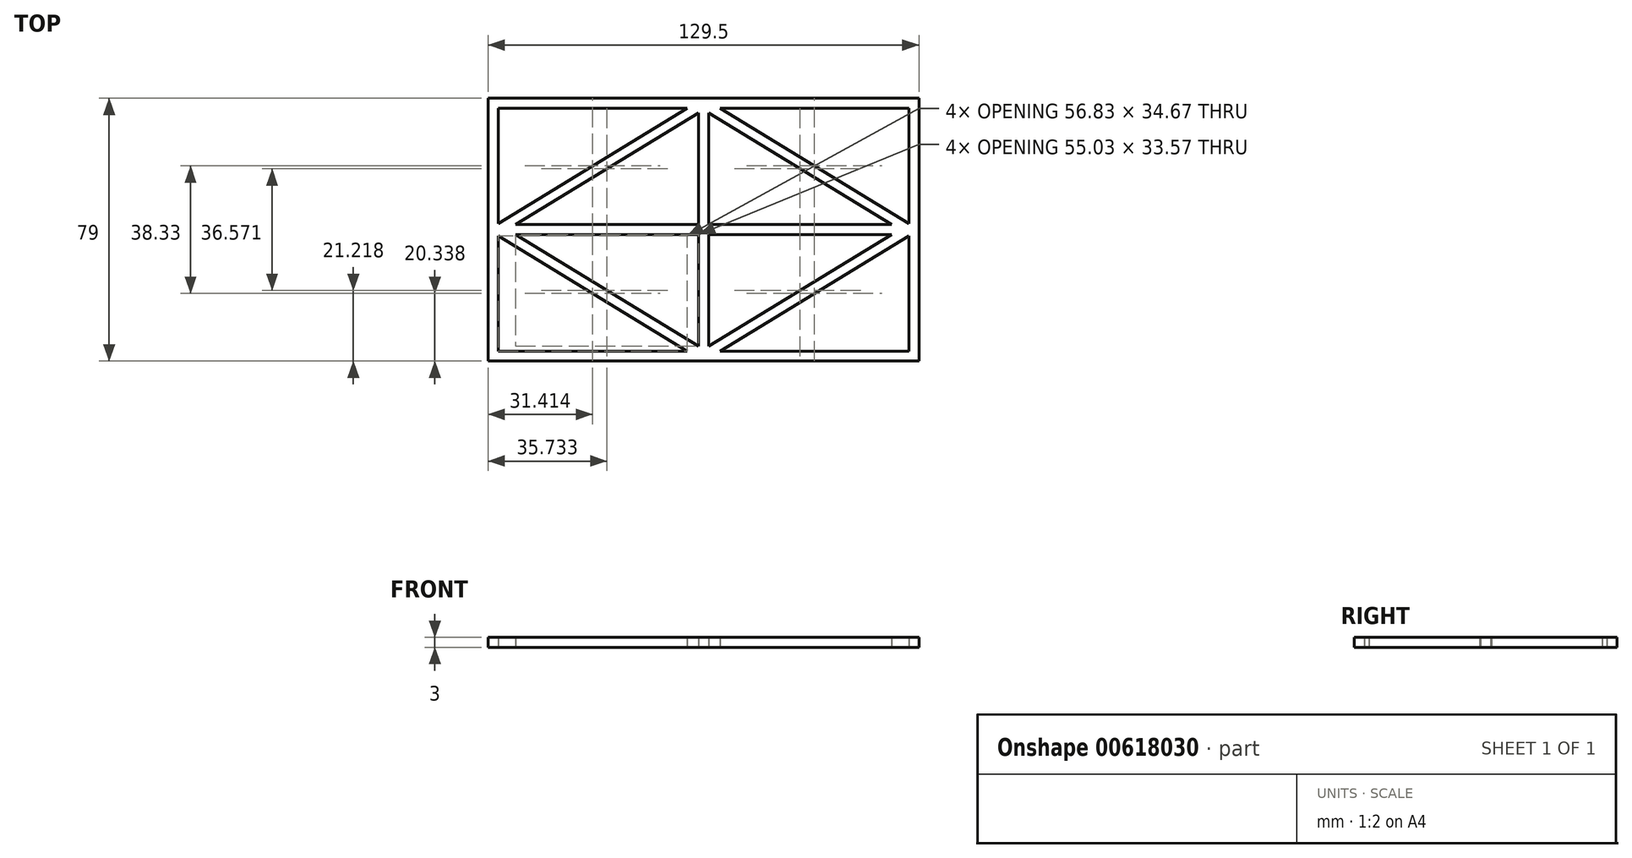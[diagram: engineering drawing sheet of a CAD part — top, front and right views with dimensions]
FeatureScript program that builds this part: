
annotation { "Feature Type Name" : "Feature", "Feature Type Description" : "" }
export const myFeature = defineFeature(function(context is Context, id is Id, definition is map)
    precondition{}
    {
        {
            var Q0;
            Q0=qCreatedBy(makeId("Top.planeOp"),FACE);
            var sketch = newSketch(context, id + "F0", { "sketchPlane" : qUnion([Q0])});
            skLineSegment(sketch, "E0.bottom", {"start": v(-93.35, 45.57) * mm, "end": v(36.15, 45.57) * mm});
            skLineSegment(sketch, "E0.top", {"start": v(-93.35, -33.43) * mm, "end": v(36.15, -33.43) * mm});
            skLineSegment(sketch, "E0.left", {"start": v(-93.35, 45.57) * mm, "end": v(-93.35, -33.43) * mm});
            skLineSegment(sketch, "E0.right", {"start": v(36.15, 45.57) * mm, "end": v(36.15, -33.43) * mm});
            skLineSegment(sketch, "E1", {"start": v(-28.6, 45.57) * mm, "end": v(-28.6, -33.43) * mm});
            skLineSegment(sketch, "E2", {"start": v(-28.6, -33.43) * mm, "end": v(-93.35, 6.07) * mm});
            skLineSegment(sketch, "E3", {"start": v(-93.35, 6.07) * mm, "end": v(-28.6, 45.57) * mm});
            skLineSegment(sketch, "E4", {"start": v(-28.6, 45.57) * mm, "end": v(36.15, 6.07) * mm});
            skLineSegment(sketch, "E5", {"start": v(36.15, 6.07) * mm, "end": v(-28.6, -33.43) * mm});
            skLineSegment(sketch, "E6", {"start": v(36.15, 6.07) * mm, "end": v(-93.35, 6.07) * mm});
            skLineSegment(sketch, "E7.0", {"start": v(-30.1, 45.57) * mm, "end": v(-30.1, -33.43) * mm});
            skLineSegment(sketch, "E8.0", {"start": v(-27.1, 45.57) * mm, "end": v(-27.1, -33.43) * mm});
            skLineSegment(sketch, "E9.0", {"start": v(36.15, 7.57) * mm, "end": v(-93.35, 7.57) * mm});
            skLineSegment(sketch, "E10.0", {"start": v(36.15, 4.57) * mm, "end": v(-93.35, 4.57) * mm});
            skLineSegment(sketch, "E11.0", {"start": v(-90.35, 42.57) * mm, "end": v(33.15, 42.57) * mm});
            skLineSegment(sketch, "E11.1", {"start": v(-90.35, 42.57) * mm, "end": v(-90.35, -30.43) * mm});
            skLineSegment(sketch, "E11.2", {"start": v(-90.35, -30.43) * mm, "end": v(33.15, -30.43) * mm});
            skLineSegment(sketch, "E11.3", {"start": v(33.15, 42.57) * mm, "end": v(33.15, -30.43) * mm});
            skLineSegment(sketch, "E12.0", {"start": v(-87.6, 6.07) * mm, "end": v(-28.6, 42.06) * mm});
            skLineSegment(sketch, "E12.1", {"start": v(-28.6, -29.91) * mm, "end": v(-87.6, 6.07) * mm});
            skLineSegment(sketch, "E12.2", {"start": v(30.39, 6.07) * mm, "end": v(-28.6, -29.91) * mm});
            skLineSegment(sketch, "E12.3", {"start": v(-28.6, 42.06) * mm, "end": v(30.39, 6.07) * mm});
            skSolve(sketch);
        }
        {
            var Q0;
            {var subQ8=sQuery(id+"F0.wireOp",EDGE,"E0.left");var subQ9=sQuery(id+"F0.wireOp",EDGE,"E0.bottom");var subQ10=makeQuery(id+"F0.imprint","INTERSECT",VERTEX,{"derivedFrom":[subQ9,subQ8]});Q0=makeQuery(id+"F0.imprint","IMPRINT",FACE,{"disambiguationData":[TD([[makeQuery(id+"F0.imprint","IMPRINT",EDGE,{"disambiguationData":[TD([[subQ10,-1.0]])],"derivedFrom":subQ9}),-1.0]])]});}
            var Q1;
            {var subQ1=sQuery(id+"F0.wireOp",EDGE,"E3");var subQ8=sQuery(id+"F0.wireOp",EDGE,"E11.1");var subQ11=makeQuery(id+"F0.imprint","INTERSECT",VERTEX,{"derivedFrom":[subQ1,subQ8]});Q1=makeQuery(id+"F0.imprint","IMPRINT",FACE,{"disambiguationData":[TD([[makeQuery(id+"F0.imprint","IMPRINT",EDGE,{"disambiguationData":[TD([[subQ11,-1.0]])],"derivedFrom":subQ1}),-1.0]])]});}
            var Q2;
            {var subQ1=sQuery(id+"F0.wireOp",EDGE,"E0.bottom");var subQ3=sQuery(id+"F0.wireOp",EDGE,"E7.0");var subQ4=makeQuery(id+"F0.imprint","INTERSECT",VERTEX,{"derivedFrom":[subQ1,subQ3]});Q2=makeQuery(id+"F0.imprint","IMPRINT",FACE,{"disambiguationData":[TD([[makeQuery(id+"F0.imprint","IMPRINT",EDGE,{"disambiguationData":[TD([[subQ4,-1.0]])],"derivedFrom":subQ3}),1.0]])]});}
            var Q3;
            {var subQ0=sQuery(id+"F0.wireOp",EDGE,"E3");var subQ5=sQuery(id+"F0.wireOp",EDGE,"E7.0");var subQ6=makeQuery(id+"F0.imprint","INTERSECT",VERTEX,{"derivedFrom":[subQ0,subQ5]});Q3=makeQuery(id+"F0.imprint","IMPRINT",FACE,{"disambiguationData":[TD([[makeQuery(id+"F0.imprint","IMPRINT",EDGE,{"disambiguationData":[TD([[subQ6,-1.0]])],"derivedFrom":subQ5}),1.0]])]});}
            var Q4;
            {var subQ0=sQuery(id+"F0.wireOp",EDGE,"E11.0");var subQ1=sQuery(id+"F0.wireOp",EDGE,"E3");var subQ2=makeQuery(id+"F0.imprint","INTERSECT",VERTEX,{"derivedFrom":[subQ1,subQ0]});Q4=makeQuery(id+"F0.imprint","IMPRINT",FACE,{"disambiguationData":[TD([[makeQuery(id+"F0.imprint","IMPRINT",EDGE,{"disambiguationData":[TD([[subQ2,-1.0]])],"derivedFrom":subQ1}),-1.0]])]});}
            var Q5;
            {var subQ3=sQuery(id+"F0.wireOp",EDGE,"E11.0");var subQ5=sQuery(id+"F0.wireOp",EDGE,"E7.0");var subQ6=makeQuery(id+"F0.imprint","INTERSECT",VERTEX,{"derivedFrom":[subQ5,subQ3]});Q5=makeQuery(id+"F0.imprint","IMPRINT",FACE,{"disambiguationData":[TD([[makeQuery(id+"F0.imprint","IMPRINT",EDGE,{"disambiguationData":[TD([[subQ6,-1.0]])],"derivedFrom":subQ5}),1.0]])]});}
            var Q6;
            {var subQ3=sQuery(id+"F0.wireOp",EDGE,"E11.0");var subQ5=sQuery(id+"F0.wireOp",EDGE,"E8.0");var subQ6=makeQuery(id+"F0.imprint","INTERSECT",VERTEX,{"derivedFrom":[subQ5,subQ3]});Q6=makeQuery(id+"F0.imprint","IMPRINT",FACE,{"disambiguationData":[TD([[makeQuery(id+"F0.imprint","IMPRINT",EDGE,{"disambiguationData":[TD([[subQ6,-1.0]])],"derivedFrom":subQ5}),-1.0]])]});}
            var Q7;
            {var subQ0=sQuery(id+"F0.wireOp",EDGE,"E4");var subQ5=sQuery(id+"F0.wireOp",EDGE,"E8.0");var subQ6=makeQuery(id+"F0.imprint","INTERSECT",VERTEX,{"derivedFrom":[subQ0,subQ5]});Q7=makeQuery(id+"F0.imprint","IMPRINT",FACE,{"disambiguationData":[TD([[makeQuery(id+"F0.imprint","IMPRINT",EDGE,{"disambiguationData":[TD([[subQ6,-1.0]])],"derivedFrom":subQ5}),-1.0]])]});}
            var Q8;
            {var subQ1=sQuery(id+"F0.wireOp",EDGE,"E0.bottom");var subQ3=sQuery(id+"F0.wireOp",EDGE,"E8.0");var subQ4=makeQuery(id+"F0.imprint","INTERSECT",VERTEX,{"derivedFrom":[subQ1,subQ3]});Q8=makeQuery(id+"F0.imprint","IMPRINT",FACE,{"disambiguationData":[TD([[makeQuery(id+"F0.imprint","IMPRINT",EDGE,{"disambiguationData":[TD([[subQ4,-1.0]])],"derivedFrom":subQ3}),-1.0]])]});}
            var Q9;
            {var subQ9=sQuery(id+"F0.wireOp",EDGE,"E0.right");var subQ10=sQuery(id+"F0.wireOp",EDGE,"E0.bottom");var subQ11=makeQuery(id+"F0.imprint","INTERSECT",VERTEX,{"derivedFrom":[subQ10,subQ9]});Q9=makeQuery(id+"F0.imprint","IMPRINT",FACE,{"disambiguationData":[TD([[makeQuery(id+"F0.imprint","IMPRINT",EDGE,{"disambiguationData":[TD([[subQ11,1.0]])],"derivedFrom":subQ10}),-1.0]])]});}
            var Q10;
            {var subQ0=sQuery(id+"F0.wireOp",EDGE,"E8.0");var subQ1=sQuery(id+"F0.wireOp",EDGE,"E4");var subQ2=makeQuery(id+"F0.imprint","INTERSECT",VERTEX,{"derivedFrom":[subQ1,subQ0]});Q10=makeQuery(id+"F0.imprint","IMPRINT",FACE,{"disambiguationData":[TD([[makeQuery(id+"F0.imprint","IMPRINT",EDGE,{"disambiguationData":[TD([[subQ2,-1.0]])],"derivedFrom":subQ1}),-1.0]])]});}
            var Q11;
            {var subQ5=sQuery(id+"F0.wireOp",EDGE,"E11.0");var subQ6=sQuery(id+"F0.wireOp",EDGE,"E4");var subQ7=makeQuery(id+"F0.imprint","INTERSECT",VERTEX,{"derivedFrom":[subQ6,subQ5]});Q11=makeQuery(id+"F0.imprint","IMPRINT",FACE,{"disambiguationData":[TD([[makeQuery(id+"F0.imprint","IMPRINT",EDGE,{"disambiguationData":[TD([[subQ7,-1.0]])],"derivedFrom":subQ6}),-1.0]])]});}
            var Q12;
            {var subQ0=sQuery(id+"F0.wireOp",EDGE,"E12.0");var subQ5=sQuery(id+"F0.wireOp",EDGE,"E7.0");var subQ6=makeQuery(id+"F0.imprint","INTERSECT",VERTEX,{"derivedFrom":[subQ5,subQ0]});Q12=makeQuery(id+"F0.imprint","IMPRINT",FACE,{"disambiguationData":[TD([[makeQuery(id+"F0.imprint","IMPRINT",EDGE,{"disambiguationData":[TD([[subQ6,-1.0]])],"derivedFrom":subQ5}),1.0]])]});}
            var Q13;
            {var subQ0=sQuery(id+"F0.wireOp",EDGE,"E12.3");var subQ5=sQuery(id+"F0.wireOp",EDGE,"E8.0");var subQ6=makeQuery(id+"F0.imprint","INTERSECT",VERTEX,{"derivedFrom":[subQ5,subQ0]});Q13=makeQuery(id+"F0.imprint","IMPRINT",FACE,{"disambiguationData":[TD([[makeQuery(id+"F0.imprint","IMPRINT",EDGE,{"disambiguationData":[TD([[subQ6,-1.0]])],"derivedFrom":subQ5}),-1.0]])]});}
            var Q14;
            {var subQ1=sQuery(id+"F0.wireOp",EDGE,"E6");var subQ3=sQuery(id+"F0.wireOp",EDGE,"E7.0");var subQ4=makeQuery(id+"F0.imprint","INTERSECT",VERTEX,{"derivedFrom":[subQ1,subQ3]});Q14=makeQuery(id+"F0.imprint","IMPRINT",FACE,{"disambiguationData":[TD([[makeQuery(id+"F0.imprint","IMPRINT",EDGE,{"disambiguationData":[TD([[subQ4,1.0]])],"derivedFrom":subQ3}),-1.0]])]});}
            var Q15;
            {var subQ1=sQuery(id+"F0.wireOp",EDGE,"E6");var subQ3=sQuery(id+"F0.wireOp",EDGE,"E7.0");var subQ4=makeQuery(id+"F0.imprint","INTERSECT",VERTEX,{"derivedFrom":[subQ1,subQ3]});Q15=makeQuery(id+"F0.imprint","IMPRINT",FACE,{"disambiguationData":[TD([[makeQuery(id+"F0.imprint","IMPRINT",EDGE,{"disambiguationData":[TD([[subQ4,-1.0]])],"derivedFrom":subQ3}),-1.0]])]});}
            var Q16;
            {var subQ0=sQuery(id+"F0.wireOp",EDGE,"E9.0");var subQ1=sQuery(id+"F0.wireOp",EDGE,"E1");var subQ2=makeQuery(id+"F0.imprint","INTERSECT",VERTEX,{"derivedFrom":[subQ1,subQ0]});Q16=makeQuery(id+"F0.imprint","IMPRINT",FACE,{"disambiguationData":[TD([[makeQuery(id+"F0.imprint","IMPRINT",EDGE,{"disambiguationData":[TD([[subQ2,-1.0]])],"derivedFrom":subQ1}),-1.0]])]});}
            var Q17;
            {var subQ0=sQuery(id+"F0.wireOp",EDGE,"E9.0");var subQ1=sQuery(id+"F0.wireOp",EDGE,"E1");var subQ2=makeQuery(id+"F0.imprint","INTERSECT",VERTEX,{"derivedFrom":[subQ1,subQ0]});Q17=makeQuery(id+"F0.imprint","IMPRINT",FACE,{"disambiguationData":[TD([[makeQuery(id+"F0.imprint","IMPRINT",EDGE,{"disambiguationData":[TD([[subQ2,-1.0]])],"derivedFrom":subQ1}),1.0]])]});}
            var Q18;
            {var subQ0=sQuery(id+"F0.wireOp",EDGE,"E6");var subQ1=sQuery(id+"F0.wireOp",EDGE,"E1");var subQ2=makeQuery(id+"F0.imprint","INTERSECT",VERTEX,{"derivedFrom":[subQ1,subQ0]});Q18=makeQuery(id+"F0.imprint","IMPRINT",FACE,{"disambiguationData":[TD([[makeQuery(id+"F0.imprint","IMPRINT",EDGE,{"disambiguationData":[TD([[subQ2,-1.0]])],"derivedFrom":subQ1}),1.0]])]});}
            var Q19;
            {var subQ0=sQuery(id+"F0.wireOp",EDGE,"E6");var subQ1=sQuery(id+"F0.wireOp",EDGE,"E1");var subQ2=makeQuery(id+"F0.imprint","INTERSECT",VERTEX,{"derivedFrom":[subQ1,subQ0]});Q19=makeQuery(id+"F0.imprint","IMPRINT",FACE,{"disambiguationData":[TD([[makeQuery(id+"F0.imprint","IMPRINT",EDGE,{"disambiguationData":[TD([[subQ2,-1.0]])],"derivedFrom":subQ1}),-1.0]])]});}
            var Q20;
            {var subQ1=sQuery(id+"F0.wireOp",EDGE,"E6");var subQ3=sQuery(id+"F0.wireOp",EDGE,"E8.0");var subQ4=makeQuery(id+"F0.imprint","INTERSECT",VERTEX,{"derivedFrom":[subQ1,subQ3]});Q20=makeQuery(id+"F0.imprint","IMPRINT",FACE,{"disambiguationData":[TD([[makeQuery(id+"F0.imprint","IMPRINT",EDGE,{"disambiguationData":[TD([[subQ4,1.0]])],"derivedFrom":subQ3}),1.0]])]});}
            var Q21;
            {var subQ1=sQuery(id+"F0.wireOp",EDGE,"E6");var subQ3=sQuery(id+"F0.wireOp",EDGE,"E8.0");var subQ4=makeQuery(id+"F0.imprint","INTERSECT",VERTEX,{"derivedFrom":[subQ1,subQ3]});Q21=makeQuery(id+"F0.imprint","IMPRINT",FACE,{"disambiguationData":[TD([[makeQuery(id+"F0.imprint","IMPRINT",EDGE,{"disambiguationData":[TD([[subQ4,-1.0]])],"derivedFrom":subQ3}),1.0]])]});}
            var Q22;
            {var subQ3=sQuery(id+"F0.wireOp",EDGE,"E10.0");var subQ5=sQuery(id+"F0.wireOp",EDGE,"E8.0");var subQ6=makeQuery(id+"F0.imprint","INTERSECT",VERTEX,{"derivedFrom":[subQ5,subQ3]});Q22=makeQuery(id+"F0.imprint","IMPRINT",FACE,{"disambiguationData":[TD([[makeQuery(id+"F0.imprint","IMPRINT",EDGE,{"disambiguationData":[TD([[subQ6,-1.0]])],"derivedFrom":subQ5}),-1.0]])]});}
            var Q23;
            {var subQ3=sQuery(id+"F0.wireOp",EDGE,"E10.0");var subQ5=sQuery(id+"F0.wireOp",EDGE,"E7.0");var subQ6=makeQuery(id+"F0.imprint","INTERSECT",VERTEX,{"derivedFrom":[subQ5,subQ3]});Q23=makeQuery(id+"F0.imprint","IMPRINT",FACE,{"disambiguationData":[TD([[makeQuery(id+"F0.imprint","IMPRINT",EDGE,{"disambiguationData":[TD([[subQ6,-1.0]])],"derivedFrom":subQ5}),1.0]])]});}
            var Q24;
            {var subQ3=sQuery(id+"F0.wireOp",EDGE,"E11.3");var subQ5=sQuery(id+"F0.wireOp",EDGE,"E9.0");var subQ6=makeQuery(id+"F0.imprint","INTERSECT",VERTEX,{"derivedFrom":[subQ5,subQ3]});Q24=makeQuery(id+"F0.imprint","IMPRINT",FACE,{"disambiguationData":[TD([[makeQuery(id+"F0.imprint","IMPRINT",EDGE,{"disambiguationData":[TD([[subQ6,-1.0]])],"derivedFrom":subQ5}),1.0]])]});}
            var Q25;
            {var subQ0=sQuery(id+"F0.wireOp",EDGE,"E11.3");var subQ1=sQuery(id+"F0.wireOp",EDGE,"E4");var subQ2=makeQuery(id+"F0.imprint","INTERSECT",VERTEX,{"derivedFrom":[subQ1,subQ0]});Q25=makeQuery(id+"F0.imprint","IMPRINT",FACE,{"disambiguationData":[TD([[makeQuery(id+"F0.imprint","IMPRINT",EDGE,{"disambiguationData":[TD([[subQ2,-1.0]])],"derivedFrom":subQ1}),-1.0]])]});}
            var Q26;
            {var subQ1=sQuery(id+"F0.wireOp",EDGE,"E4");var subQ3=sQuery(id+"F0.wireOp",EDGE,"E9.0");var subQ4=makeQuery(id+"F0.imprint","INTERSECT",VERTEX,{"derivedFrom":[subQ1,subQ3]});Q26=makeQuery(id+"F0.imprint","IMPRINT",FACE,{"disambiguationData":[TD([[makeQuery(id+"F0.imprint","IMPRINT",EDGE,{"disambiguationData":[TD([[subQ4,-1.0]])],"derivedFrom":subQ3}),1.0]])]});}
            var Q27;
            {var subQ1=sQuery(id+"F0.wireOp",EDGE,"E0.right");var subQ3=sQuery(id+"F0.wireOp",EDGE,"E9.0");var subQ4=makeQuery(id+"F0.imprint","INTERSECT",VERTEX,{"derivedFrom":[subQ1,subQ3]});Q27=makeQuery(id+"F0.imprint","IMPRINT",FACE,{"disambiguationData":[TD([[makeQuery(id+"F0.imprint","IMPRINT",EDGE,{"disambiguationData":[TD([[subQ4,-1.0]])],"derivedFrom":subQ3}),1.0]])]});}
            var Q28;
            {var subQ1=sQuery(id+"F0.wireOp",EDGE,"E5");var subQ3=sQuery(id+"F0.wireOp",EDGE,"E10.0");var subQ4=makeQuery(id+"F0.imprint","INTERSECT",VERTEX,{"derivedFrom":[subQ1,subQ3]});Q28=makeQuery(id+"F0.imprint","IMPRINT",FACE,{"disambiguationData":[TD([[makeQuery(id+"F0.imprint","IMPRINT",EDGE,{"disambiguationData":[TD([[subQ4,-1.0]])],"derivedFrom":subQ3}),-1.0]])]});}
            var Q29;
            {var subQ1=sQuery(id+"F0.wireOp",EDGE,"E0.right");var subQ3=sQuery(id+"F0.wireOp",EDGE,"E10.0");var subQ4=makeQuery(id+"F0.imprint","INTERSECT",VERTEX,{"derivedFrom":[subQ1,subQ3]});Q29=makeQuery(id+"F0.imprint","IMPRINT",FACE,{"disambiguationData":[TD([[makeQuery(id+"F0.imprint","IMPRINT",EDGE,{"disambiguationData":[TD([[subQ4,-1.0]])],"derivedFrom":subQ3}),-1.0]])]});}
            var Q30;
            {var subQ3=sQuery(id+"F0.wireOp",EDGE,"E11.3");var subQ5=sQuery(id+"F0.wireOp",EDGE,"E10.0");var subQ6=makeQuery(id+"F0.imprint","INTERSECT",VERTEX,{"derivedFrom":[subQ5,subQ3]});Q30=makeQuery(id+"F0.imprint","IMPRINT",FACE,{"disambiguationData":[TD([[makeQuery(id+"F0.imprint","IMPRINT",EDGE,{"disambiguationData":[TD([[subQ6,-1.0]])],"derivedFrom":subQ5}),-1.0]])]});}
            var Q31;
            {var subQ1=sQuery(id+"F0.wireOp",EDGE,"E5");var subQ5=sQuery(id+"F0.wireOp",EDGE,"E11.3");var subQ11=makeQuery(id+"F0.imprint","INTERSECT",VERTEX,{"derivedFrom":[subQ1,subQ5]});Q31=makeQuery(id+"F0.imprint","IMPRINT",FACE,{"disambiguationData":[TD([[makeQuery(id+"F0.imprint","IMPRINT",EDGE,{"disambiguationData":[TD([[subQ11,-1.0]])],"derivedFrom":subQ1}),-1.0]])]});}
            var Q32;
            {var subQ0=sQuery(id+"F0.wireOp",EDGE,"E10.0");var subQ1=sQuery(id+"F0.wireOp",EDGE,"E5");var subQ2=makeQuery(id+"F0.imprint","INTERSECT",VERTEX,{"derivedFrom":[subQ1,subQ0]});Q32=makeQuery(id+"F0.imprint","IMPRINT",FACE,{"disambiguationData":[TD([[makeQuery(id+"F0.imprint","IMPRINT",EDGE,{"disambiguationData":[TD([[subQ2,-1.0]])],"derivedFrom":subQ1}),-1.0]])]});}
            var Q33;
            {var subQ5=sQuery(id+"F0.wireOp",EDGE,"E0.right");var subQ6=sQuery(id+"F0.wireOp",EDGE,"E0.top");var subQ7=makeQuery(id+"F0.imprint","INTERSECT",VERTEX,{"derivedFrom":[subQ6,subQ5]});Q33=makeQuery(id+"F0.imprint","IMPRINT",FACE,{"disambiguationData":[TD([[makeQuery(id+"F0.imprint","IMPRINT",EDGE,{"disambiguationData":[TD([[subQ7,1.0]])],"derivedFrom":subQ6}),1.0]])]});}
            var Q34;
            {var subQ1=sQuery(id+"F0.wireOp",EDGE,"E0.top");var subQ3=sQuery(id+"F0.wireOp",EDGE,"E8.0");var subQ4=makeQuery(id+"F0.imprint","INTERSECT",VERTEX,{"derivedFrom":[subQ1,subQ3]});Q34=makeQuery(id+"F0.imprint","IMPRINT",FACE,{"disambiguationData":[TD([[makeQuery(id+"F0.imprint","IMPRINT",EDGE,{"disambiguationData":[TD([[subQ4,1.0]])],"derivedFrom":subQ3}),-1.0]])]});}
            var Q35;
            {var subQ0=sQuery(id+"F0.wireOp",EDGE,"E5");var subQ5=sQuery(id+"F0.wireOp",EDGE,"E8.0");var subQ6=makeQuery(id+"F0.imprint","INTERSECT",VERTEX,{"derivedFrom":[subQ0,subQ5]});Q35=makeQuery(id+"F0.imprint","IMPRINT",FACE,{"disambiguationData":[TD([[makeQuery(id+"F0.imprint","IMPRINT",EDGE,{"disambiguationData":[TD([[subQ6,1.0]])],"derivedFrom":subQ5}),-1.0]])]});}
            var Q36;
            {var subQ0=sQuery(id+"F0.wireOp",EDGE,"E11.2");var subQ1=sQuery(id+"F0.wireOp",EDGE,"E5");var subQ2=makeQuery(id+"F0.imprint","INTERSECT",VERTEX,{"derivedFrom":[subQ1,subQ0]});Q36=makeQuery(id+"F0.imprint","IMPRINT",FACE,{"disambiguationData":[TD([[makeQuery(id+"F0.imprint","IMPRINT",EDGE,{"disambiguationData":[TD([[subQ2,-1.0]])],"derivedFrom":subQ1}),-1.0]])]});}
            var Q37;
            {var subQ0=sQuery(id+"F0.wireOp",EDGE,"E12.2");var subQ5=sQuery(id+"F0.wireOp",EDGE,"E8.0");var subQ7=makeQuery(id+"F0.imprint","INTERSECT",VERTEX,{"derivedFrom":[subQ5,subQ0]});Q37=makeQuery(id+"F0.imprint","IMPRINT",FACE,{"disambiguationData":[TD([[makeQuery(id+"F0.imprint","IMPRINT",EDGE,{"disambiguationData":[TD([[subQ7,-1.0]])],"derivedFrom":subQ5}),-1.0]])]});}
            var Q38;
            {var subQ0=sQuery(id+"F0.wireOp",EDGE,"E12.1");var subQ5=sQuery(id+"F0.wireOp",EDGE,"E7.0");var subQ6=makeQuery(id+"F0.imprint","INTERSECT",VERTEX,{"derivedFrom":[subQ5,subQ0]});Q38=makeQuery(id+"F0.imprint","IMPRINT",FACE,{"disambiguationData":[TD([[makeQuery(id+"F0.imprint","IMPRINT",EDGE,{"disambiguationData":[TD([[subQ6,-1.0]])],"derivedFrom":subQ5}),1.0]])]});}
            var Q39;
            {var subQ0=sQuery(id+"F0.wireOp",EDGE,"E2");var subQ5=sQuery(id+"F0.wireOp",EDGE,"E7.0");var subQ6=makeQuery(id+"F0.imprint","INTERSECT",VERTEX,{"derivedFrom":[subQ0,subQ5]});Q39=makeQuery(id+"F0.imprint","IMPRINT",FACE,{"disambiguationData":[TD([[makeQuery(id+"F0.imprint","IMPRINT",EDGE,{"disambiguationData":[TD([[subQ6,1.0]])],"derivedFrom":subQ5}),1.0]])]});}
            var Q40;
            {var subQ1=sQuery(id+"F0.wireOp",EDGE,"E0.top");var subQ3=sQuery(id+"F0.wireOp",EDGE,"E7.0");var subQ4=makeQuery(id+"F0.imprint","INTERSECT",VERTEX,{"derivedFrom":[subQ1,subQ3]});Q40=makeQuery(id+"F0.imprint","IMPRINT",FACE,{"disambiguationData":[TD([[makeQuery(id+"F0.imprint","IMPRINT",EDGE,{"disambiguationData":[TD([[subQ4,1.0]])],"derivedFrom":subQ3}),1.0]])]});}
            var Q41;
            {var subQ10=sQuery(id+"F0.wireOp",EDGE,"E0.left");var subQ12=sQuery(id+"F0.wireOp",EDGE,"E0.top");var subQ13=makeQuery(id+"F0.imprint","INTERSECT",VERTEX,{"derivedFrom":[subQ12,subQ10]});Q41=makeQuery(id+"F0.imprint","IMPRINT",FACE,{"disambiguationData":[TD([[makeQuery(id+"F0.imprint","IMPRINT",EDGE,{"disambiguationData":[TD([[subQ13,-1.0]])],"derivedFrom":subQ12}),1.0]])]});}
            var Q42;
            {var subQ0=sQuery(id+"F0.wireOp",EDGE,"E7.0");var subQ1=sQuery(id+"F0.wireOp",EDGE,"E2");var subQ2=makeQuery(id+"F0.imprint","INTERSECT",VERTEX,{"derivedFrom":[subQ1,subQ0]});Q42=makeQuery(id+"F0.imprint","IMPRINT",FACE,{"disambiguationData":[TD([[makeQuery(id+"F0.imprint","IMPRINT",EDGE,{"disambiguationData":[TD([[subQ2,-1.0]])],"derivedFrom":subQ1}),-1.0]])]});}
            var Q43;
            {var subQ1=sQuery(id+"F0.wireOp",EDGE,"E2");var subQ9=sQuery(id+"F0.wireOp",EDGE,"E11.2");var subQ11=makeQuery(id+"F0.imprint","INTERSECT",VERTEX,{"derivedFrom":[subQ1,subQ9]});Q43=makeQuery(id+"F0.imprint","IMPRINT",FACE,{"disambiguationData":[TD([[makeQuery(id+"F0.imprint","IMPRINT",EDGE,{"disambiguationData":[TD([[subQ11,-1.0]])],"derivedFrom":subQ1}),-1.0]])]});}
            var Q44;
            {var subQ0=sQuery(id+"F0.wireOp",EDGE,"E9.0");var subQ1=sQuery(id+"F0.wireOp",EDGE,"E3");var subQ2=makeQuery(id+"F0.imprint","INTERSECT",VERTEX,{"derivedFrom":[subQ1,subQ0]});Q44=makeQuery(id+"F0.imprint","IMPRINT",FACE,{"disambiguationData":[TD([[makeQuery(id+"F0.imprint","IMPRINT",EDGE,{"disambiguationData":[TD([[subQ2,-1.0]])],"derivedFrom":subQ1}),-1.0]])]});}
            var Q45;
            {var subQ0=sQuery(id+"F0.wireOp",EDGE,"E11.1");var subQ1=sQuery(id+"F0.wireOp",EDGE,"E2");var subQ2=makeQuery(id+"F0.imprint","INTERSECT",VERTEX,{"derivedFrom":[subQ1,subQ0]});Q45=makeQuery(id+"F0.imprint","IMPRINT",FACE,{"disambiguationData":[TD([[makeQuery(id+"F0.imprint","IMPRINT",EDGE,{"disambiguationData":[TD([[subQ2,-1.0]])],"derivedFrom":subQ1}),-1.0]])]});}
            var Q46;
            {var subQ0=sQuery(id+"F0.wireOp",EDGE,"E12.1");var subQ5=sQuery(id+"F0.wireOp",EDGE,"E10.0");var subQ6=makeQuery(id+"F0.imprint","INTERSECT",VERTEX,{"derivedFrom":[subQ5,subQ0]});Q46=makeQuery(id+"F0.imprint","IMPRINT",FACE,{"disambiguationData":[TD([[makeQuery(id+"F0.imprint","IMPRINT",EDGE,{"disambiguationData":[TD([[subQ6,-1.0]])],"derivedFrom":subQ5}),-1.0]])]});}
            var Q47;
            {var subQ0=sQuery(id+"F0.wireOp",EDGE,"E12.0");var subQ5=sQuery(id+"F0.wireOp",EDGE,"E9.0");var subQ7=makeQuery(id+"F0.imprint","INTERSECT",VERTEX,{"derivedFrom":[subQ5,subQ0]});Q47=makeQuery(id+"F0.imprint","IMPRINT",FACE,{"disambiguationData":[TD([[makeQuery(id+"F0.imprint","IMPRINT",EDGE,{"disambiguationData":[TD([[subQ7,-1.0]])],"derivedFrom":subQ5}),1.0]])]});}
            var Q48;
            {var subQ1=sQuery(id+"F0.wireOp",EDGE,"E3");var subQ3=sQuery(id+"F0.wireOp",EDGE,"E9.0");var subQ4=makeQuery(id+"F0.imprint","INTERSECT",VERTEX,{"derivedFrom":[subQ1,subQ3]});Q48=makeQuery(id+"F0.imprint","IMPRINT",FACE,{"disambiguationData":[TD([[makeQuery(id+"F0.imprint","IMPRINT",EDGE,{"disambiguationData":[TD([[subQ4,1.0]])],"derivedFrom":subQ3}),1.0]])]});}
            var Q49;
            {var subQ1=sQuery(id+"F0.wireOp",EDGE,"E2");var subQ3=sQuery(id+"F0.wireOp",EDGE,"E10.0");var subQ4=makeQuery(id+"F0.imprint","INTERSECT",VERTEX,{"derivedFrom":[subQ1,subQ3]});Q49=makeQuery(id+"F0.imprint","IMPRINT",FACE,{"disambiguationData":[TD([[makeQuery(id+"F0.imprint","IMPRINT",EDGE,{"disambiguationData":[TD([[subQ4,1.0]])],"derivedFrom":subQ3}),-1.0]])]});}
            var Q50;
            {var subQ1=sQuery(id+"F0.wireOp",EDGE,"E0.left");var subQ3=sQuery(id+"F0.wireOp",EDGE,"E10.0");var subQ4=makeQuery(id+"F0.imprint","INTERSECT",VERTEX,{"derivedFrom":[subQ1,subQ3]});Q50=makeQuery(id+"F0.imprint","IMPRINT",FACE,{"disambiguationData":[TD([[makeQuery(id+"F0.imprint","IMPRINT",EDGE,{"disambiguationData":[TD([[subQ4,1.0]])],"derivedFrom":subQ3}),-1.0]])]});}
            var Q51;
            {var subQ1=sQuery(id+"F0.wireOp",EDGE,"E0.left");var subQ3=sQuery(id+"F0.wireOp",EDGE,"E9.0");var subQ4=makeQuery(id+"F0.imprint","INTERSECT",VERTEX,{"derivedFrom":[subQ1,subQ3]});Q51=makeQuery(id+"F0.imprint","IMPRINT",FACE,{"disambiguationData":[TD([[makeQuery(id+"F0.imprint","IMPRINT",EDGE,{"disambiguationData":[TD([[subQ4,1.0]])],"derivedFrom":subQ3}),1.0]])]});}
            extrude(context, id + "F1", {"entities" : qUnion([Q0, Q1, Q2, Q3, Q4, Q5, Q6, Q7, Q8, Q9, Q10, Q11, Q12, Q13, Q14, Q15, Q16, Q17, Q18, Q19, Q20, Q21, Q22, Q23, Q24, Q25, Q26, Q27, Q28, Q29, Q30, Q31, Q32, Q33, Q34, Q35, Q36, Q37, Q38, Q39, Q40, Q41, Q42, Q43, Q44, Q45, Q46, Q47, Q48, Q49, Q50, Q51]), "depth" : 3 * mm, "offsetDistance" : 25 * mm});
        }
    });
